# Revit family: Magnuson-Stilla-Outdoor_Seating
name_source: partatom
category: Furniture
units: mm (PartAtom-declared; Revit-internal decimal feet)

## family parameters
Always vertical = Yes
Cut with Voids When Loaded = No
OmniClass Number = 23.40.20.00
OmniClass Title = General Furniture and Specialties
Room Calculation Point = No
Shared = No
Work Plane-Based = No

## types (1)
- STIL-CHR
    Assembly Code = E2020200
    Default Elevation = 0"
    Depth = 20 1/4"
    Description = Polypropylene and fiber glass chair with cut out for rainwater drain off. Stackable 6 units high for storage. Ships assembled. Suitable for indoor and outdoor use. Sold in Cartons of 4 only.
    Height = 30 3/4"
    Keynote = 12500
    Manufacturer = Magnuson Group
    Model = STIL-CHR
    Product Documentation Link = https://www.magnusongroup.com
    Revit Model Built By = https://www.servex-us.com
    Seat Finish = MGA - Plastic White
    Type Comments = Stilla Chair
    URL = www.magnusongroup.com
    Width = 21"

## geometry (parser evidence)
native form markers: Sweep x2
no freeform markers — native parametric forms only
